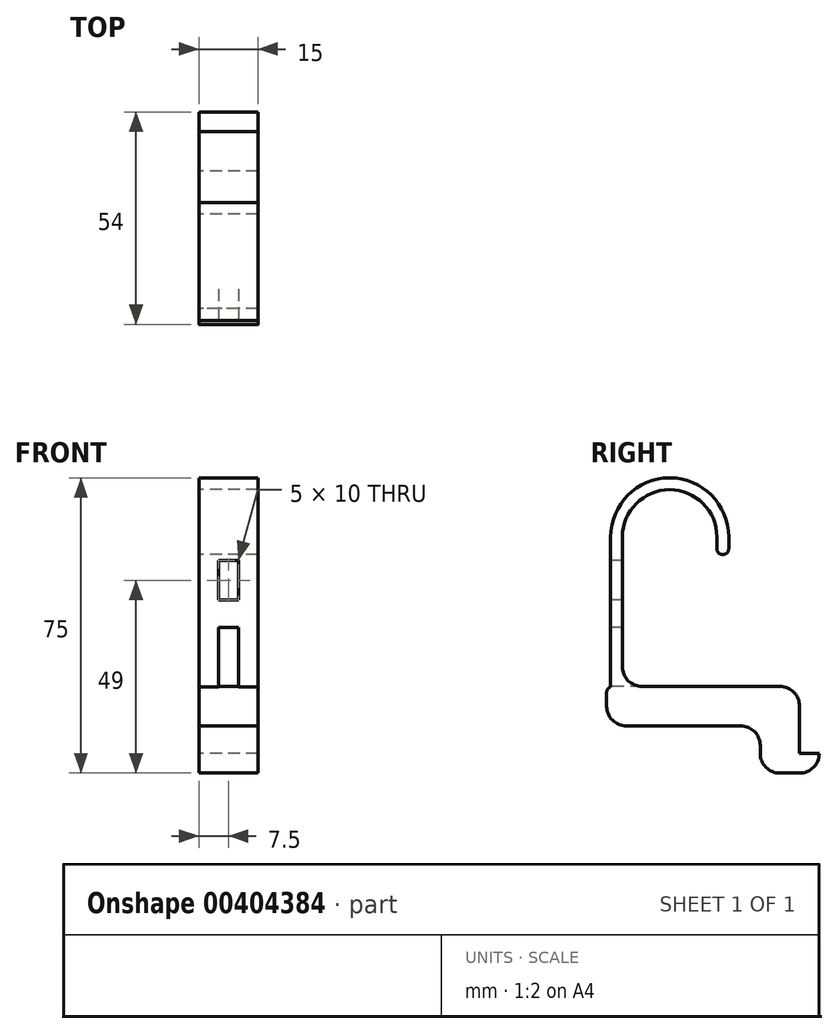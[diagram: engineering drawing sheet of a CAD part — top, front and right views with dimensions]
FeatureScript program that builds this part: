
annotation { "Feature Type Name" : "Feature", "Feature Type Description" : "" }
export const myFeature = defineFeature(function(context is Context, id is Id, definition is map)
    precondition{}
    {
        {
            var Q0;
            Q0=qCreatedBy(makeId("Right.planeOp"),FACE);
            var sketch = newSketch(context, id + "F0", { "sketchPlane" : qUnion([Q0])});
            skArc(sketch, "E0", {"start": v(12, 0) * mm, "mid": v(0, 12) * mm, "end": v(-12, 0) * mm});
            skArc(sketch, "E1", {"start": v(-15, 0) * mm, "mid": v(0, 15) * mm, "end": v(15, 0) * mm});
            skLineSegment(sketch, "E2.left", {"start": v(12, 0) * mm, "end": v(12, -3) * mm});
            skLineSegment(sketch, "E2.right", {"start": v(15, 0) * mm, "end": v(15, -3) * mm});
            skArc(sketch, "E3", {"start": v(12, -3) * mm, "mid": v(13.5, -4.5) * mm, "end": v(15, -3) * mm});
            skLineSegment(sketch, "E4.top", {"start": v(-15, -48) * mm, "end": v(-12, -48) * mm});
            skLineSegment(sketch, "E4.left", {"start": v(-15, 0) * mm, "end": v(-15, -48) * mm});
            skLineSegment(sketch, "E4.right", {"start": v(-12, 0) * mm, "end": v(-12, -38) * mm});
            skLineSegment(sketch, "E5.bottom", {"start": v(-12, -48) * mm, "end": v(23, -48) * mm});
            skLineSegment(sketch, "E5.top", {"start": v(-12, -38) * mm, "end": v(33, -38) * mm});
            skLineSegment(sketch, "E5.right", {"start": v(33, -48) * mm, "end": v(33, -38) * mm});
            skLineSegment(sketch, "E6.top", {"start": v(23, -60) * mm, "end": v(33, -60) * mm});
            skLineSegment(sketch, "E6.left", {"start": v(23, -48) * mm, "end": v(23, -60) * mm});
            skLineSegment(sketch, "E6.right", {"start": v(33, -48) * mm, "end": v(33, -55) * mm});
            skLineSegment(sketch, "E7.bottom", {"start": v(33, -60) * mm, "end": v(38, -60) * mm});
            skLineSegment(sketch, "E7.top", {"start": v(33, -55) * mm, "end": v(38, -55) * mm});
            skLineSegment(sketch, "E7.right", {"start": v(38, -60) * mm, "end": v(38, -55) * mm});
            skLineSegment(sketch, "E8", {"start": v(-15, -48) * mm, "end": v(-16, -48) * mm});
            skLineSegment(sketch, "E9", {"start": v(-16, -48) * mm, "end": v(-16, -38) * mm});
            skLineSegment(sketch, "E10", {"start": v(-16, -38) * mm, "end": v(-15, -38) * mm});
            skSolve(sketch);
        }
        {
            var Q0;
            Q0 = qSketchRegion(id + "F0", true);
            extrude(context, id + "F1", {"entities" : qUnion([Q0]), "depth" : 7.5 * mm, "hasSecondDirection" : true, "secondDirectionOppositeDirection" : true, "secondDirectionDepth" : 7.5 * mm});
        }
        {
            var Q0;
            Q0=makeQuery(id+"F1.opExtrude","SWEPT_FACE",FACE,{"disambiguationData":[OSD([sQuery(id+"F0.wireOp",EDGE,"E4.left")])]});
            var sketch = newSketch(context, id + "F2", { "sketchPlane" : qUnion([Q0])});
            skLineSegment(sketch, "E11.bottom", {"start": v(2.5, -6) * mm, "end": v(-2.5, -6) * mm});
            skLineSegment(sketch, "E11.top", {"start": v(2.5, -16) * mm, "end": v(-2.5, -16) * mm});
            skLineSegment(sketch, "E11.left", {"start": v(2.5, -6) * mm, "end": v(2.5, -16) * mm});
            skLineSegment(sketch, "E11.right", {"start": v(-2.5, -6) * mm, "end": v(-2.5, -16) * mm});
            skPoint(sketch, "E11.middle", {"position": v(0, -11) * mm});
            skLineSegment(sketch, "E12.bottom", {"start": v(2.5, -23) * mm, "end": v(-2.5, -23) * mm});
            skLineSegment(sketch, "E12.top", {"start": v(2.5, -38) * mm, "end": v(-2.5, -38) * mm});
            skLineSegment(sketch, "E12.left", {"start": v(2.5, -23) * mm, "end": v(2.5, -38) * mm});
            skLineSegment(sketch, "E12.right", {"start": v(-2.5, -23) * mm, "end": v(-2.5, -38) * mm});
            skPoint(sketch, "E12.middle", {"position": v(0, -30.5) * mm});
            skSolve(sketch);
        }
        {
            var Q0;
            Q0 = qSketchRegion(id + "F2", true);
            extrude(context, id + "F3", {"entities" : qUnion([Q0]), "operationType" : NewBodyOperationType.REMOVE, "endBound" : BoundingType.UP_TO_NEXT, "oppositeDirection" : true, "depth" : 25 * mm});
        }
        {
            var Q0;
            Q0=makeQuery(id+"F3.boolean.opBoolean","COPY",EDGE,{"derivedFrom":makeQuery(id+"F3.opExtrude","CAP_EDGE",EDGE,{"disambiguationData":[OSD([sQuery(id+"F2.wireOp",EDGE,"E11.bottom")])],"isStart":true})});
            var Q1;
            Q1=makeQuery(id+"F3.boolean.opBoolean","COPY",EDGE,{"derivedFrom":makeQuery(id+"F3.opExtrude","CAP_EDGE",EDGE,{"disambiguationData":[OSD([sQuery(id+"F2.wireOp",EDGE,"E11.bottom")])],"isStart":false})});
            var Q2;
            Q2=makeQuery(id+"F3.boolean.opBoolean","COPY",EDGE,{"derivedFrom":makeQuery(id+"F3.opExtrude","CAP_EDGE",EDGE,{"disambiguationData":[OSD([sQuery(id+"F2.wireOp",EDGE,"E12.bottom")])],"isStart":true})});
            var Q3;
            Q3=makeQuery(id+"F3.boolean.opBoolean","COPY",EDGE,{"derivedFrom":makeQuery(id+"F3.opExtrude","CAP_EDGE",EDGE,{"disambiguationData":[OSD([sQuery(id+"F2.wireOp",EDGE,"E12.bottom")])],"isStart":false})});
            var Q4;
            Q4=makeQuery(id+"F1.opExtrude","SWEPT_EDGE",EDGE,{"disambiguationData":[OSD([sQuery(id+"F0.wireOp",EDGE,"E9"),sQuery(id+"F0.wireOp",EDGE,"E10")])]});
            fillet(context, id + "F4", {"entities" : qUnion([Q0, Q1, Q2, Q3, Q4]), "radius" : 1.5 * mm, "tangentPropagation" : true, "allowEdgeOverflow" : false});
        }
        {
            var Q0;
            {var subQ0=sQuery(id+"F0.wireOp",EDGE,"E5.top");var subQ1=sQuery(id+"F0.wireOp",EDGE,"E4.right");Q0=makeQuery(id+"F3.boolean.opBoolean","SPLIT",EDGE,{"disambiguationData":[TD([makeQuery(id+"F3.opExtrude","SWEPT_FACE",FACE,{"disambiguationData":[OSD([sQuery(id+"F2.wireOp",EDGE,"E12.left")])]})])],"derivedFrom":makeQuery(id+"F1.opExtrude","SWEPT_EDGE",EDGE,{"disambiguationData":[OSD([subQ1,subQ0])]})});}
            var Q1;
            {var subQ1=sQuery(id+"F0.wireOp",EDGE,"E5.top");var subQ2=sQuery(id+"F0.wireOp",EDGE,"E4.right");Q1=makeQuery(id+"F3.boolean.opBoolean","SPLIT",EDGE,{"disambiguationData":[TD([makeQuery(id+"F3.opExtrude","SWEPT_FACE",FACE,{"disambiguationData":[OSD([sQuery(id+"F2.wireOp",EDGE,"E12.right")])]})])],"derivedFrom":makeQuery(id+"F1.opExtrude","SWEPT_EDGE",EDGE,{"disambiguationData":[OSD([subQ2,subQ1])]})});}
            var Q2;
            Q2=makeQuery(id+"F1.opExtrude","SWEPT_EDGE",EDGE,{"disambiguationData":[OSD([sQuery(id+"F0.wireOp",EDGE,"E5.top"),sQuery(id+"F0.wireOp",EDGE,"E5.right")])]});
            var Q3;
            Q3=makeQuery(id+"F1.opExtrude","SWEPT_EDGE",EDGE,{"disambiguationData":[OSD([sQuery(id+"F0.wireOp",EDGE,"E7.bottom"),sQuery(id+"F0.wireOp",EDGE,"E7.right")])]});
            var Q4;
            Q4=makeQuery(id+"F1.opExtrude","SWEPT_EDGE",EDGE,{"disambiguationData":[OSD([sQuery(id+"F0.wireOp",EDGE,"E6.top"),sQuery(id+"F0.wireOp",EDGE,"E6.left")])]});
            var Q5;
            Q5=makeQuery(id+"F1.opExtrude","SWEPT_EDGE",EDGE,{"disambiguationData":[OSD([sQuery(id+"F0.wireOp",EDGE,"E5.bottom"),sQuery(id+"F0.wireOp",EDGE,"E6.left")])]});
            var Q6;
            Q6=makeQuery(id+"F1.opExtrude","SWEPT_EDGE",EDGE,{"disambiguationData":[OSD([sQuery(id+"F0.wireOp",EDGE,"E1"),sQuery(id+"F0.wireOp",EDGE,"E4.left")])]});
            var Q7;
            Q7=makeQuery(id+"F1.opExtrude","SWEPT_EDGE",EDGE,{"disambiguationData":[OSD([sQuery(id+"F0.wireOp",EDGE,"E8"),sQuery(id+"F0.wireOp",EDGE,"E9")])]});
            fillet(context, id + "F5", {"entities" : qUnion([Q0, Q1, Q2, Q3, Q4, Q5, Q6, Q7]), "radius" : 5 * mm, "tangentPropagation" : true, "allowEdgeOverflow" : false});
        }
    });
